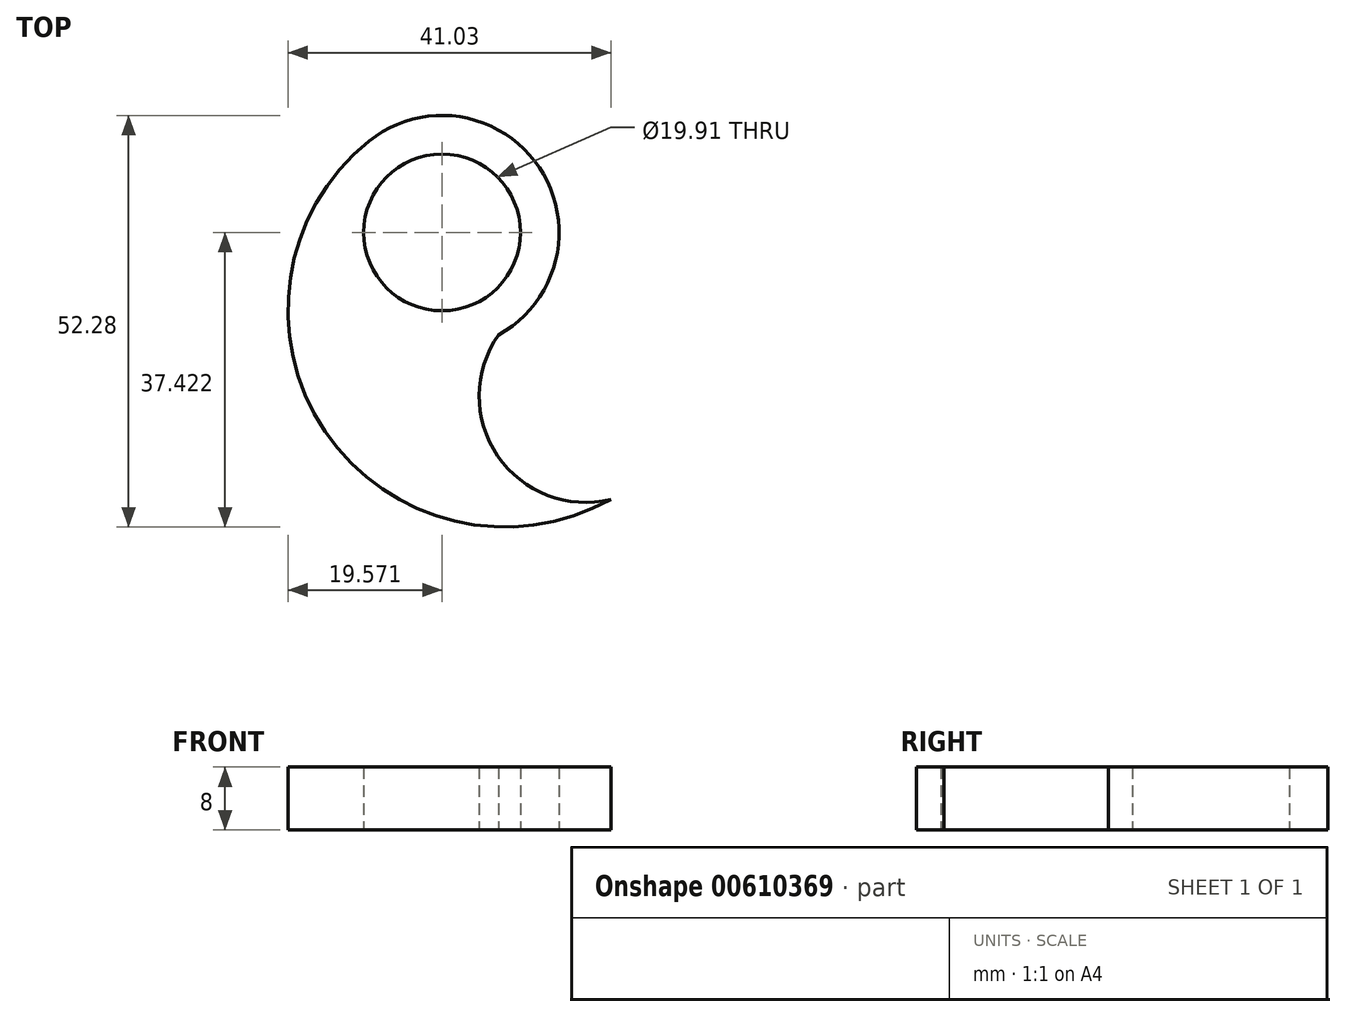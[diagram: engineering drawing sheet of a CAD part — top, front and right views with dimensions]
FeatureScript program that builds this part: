
annotation { "Feature Type Name" : "Feature", "Feature Type Description" : "" }
export const myFeature = defineFeature(function(context is Context, id is Id, definition is map)
    precondition{}
    {
        {
            var Q0;
            Q0=qCreatedBy(makeId("Top.planeOp"),FACE);
            var sketch = newSketch(context, id + "F0", { "sketchPlane" : qUnion([Q0])});
            skCircle(sketch, "E0", {"center": v(22.7, 20.78) * mm, "radius": 9.95 * mm});
            skCircle(sketch, "E1", {"center": v(22.7, 20.78) * mm, "radius": 14.86 * mm});
            skArc(sketch, "E2", {"start": v(13.44, 32.41) * mm, "mid": v(7.83, -4.49) * mm, "end": v(44.15, -13.12) * mm});
            skArc(sketch, "E3", {"start": v(29.87, 7.77) * mm, "mid": v(29.77, -7.62) * mm, "end": v(44.15, -13.12) * mm});
            skLineSegment(sketch, "E4", {"start": v(44.15, -13.12) * mm, "end": v(44.15, -13.12) * mm});
            skSolve(sketch);
        }
        {
            var Q0;
            Q0=qCreatedBy(makeId("Top.planeOp"),FACE);
            var sketch = newSketch(context, id + "F1", { "sketchPlane" : qUnion([Q0])});
            skSolve(sketch);
        }
        {
            var Q0;
            Q0 = qSketchRegion(id + "F1", true);
            var Q1;
            Q1=makeQuery(id+"F0.imprint","IMPRINT",FACE,{"disambiguationData":[TD([[makeQuery(id+"F0.imprint","IMPRINT",EDGE,{"derivedFrom":sQuery(id+"F0.wireOp",EDGE,"E0")}),-1.0]])]});
            var Q2;
            {var subQ0=sQuery(id+"F0.wireOp",EDGE,"E2");Q2=makeQuery(id+"F0.imprint","IMPRINT",FACE,{"disambiguationData":[TD([[makeQuery(id+"F0.imprint","IMPRINT",EDGE,{"derivedFrom":subQ0}),1.0]])]});}
            extrude(context, id + "F2", {"entities" : qUnion([Q0, Q1, Q2]), "depth" : 8 * mm, "offsetDistance" : 25 * mm});
        }
    });
